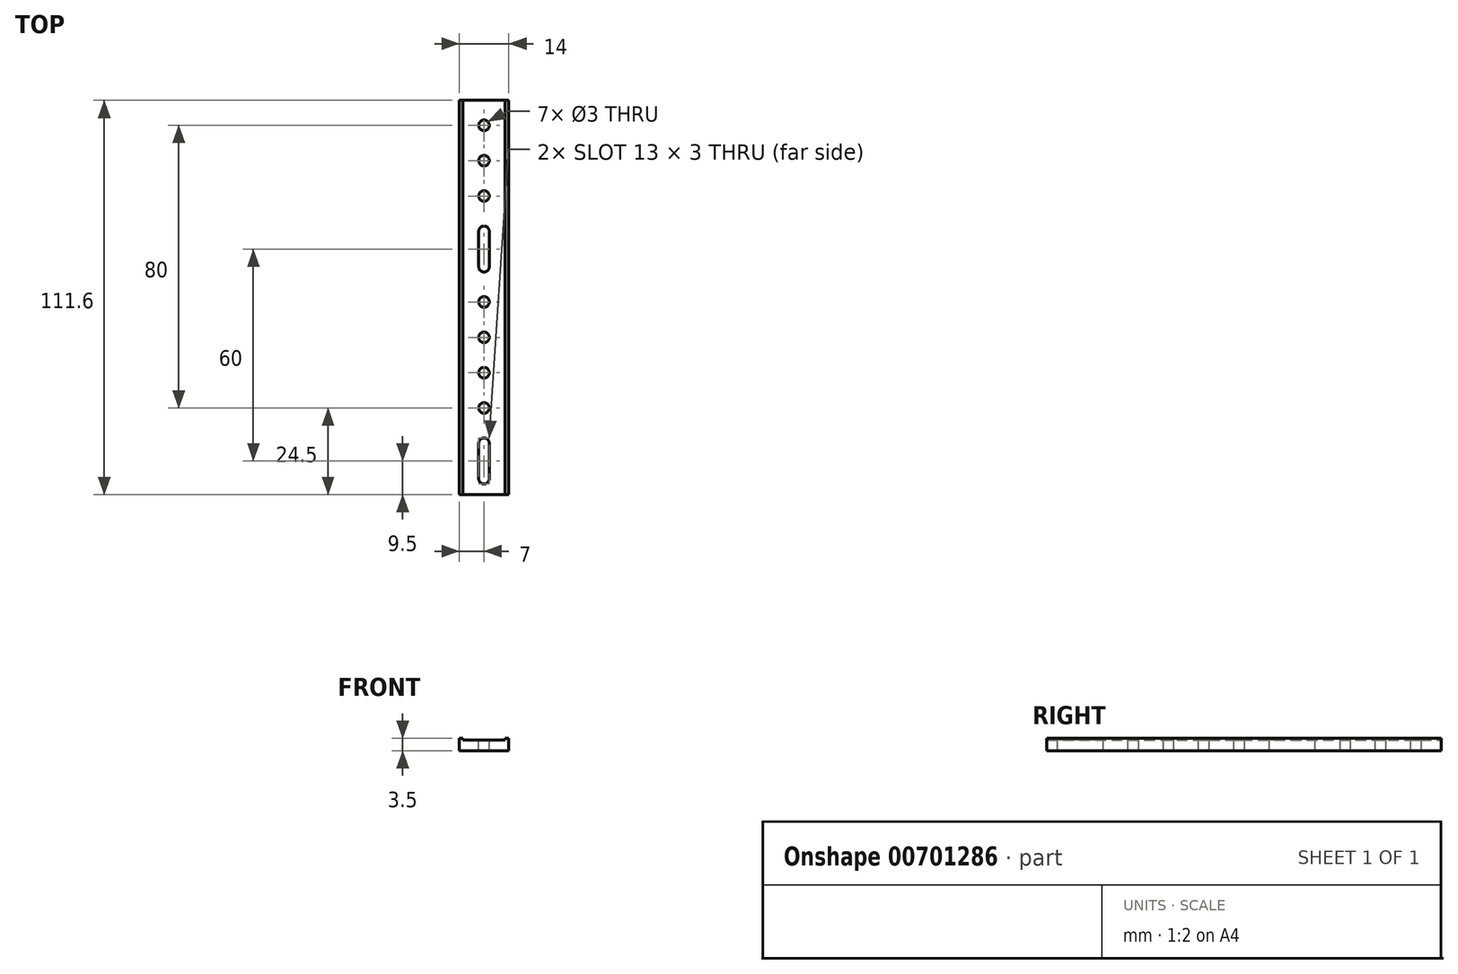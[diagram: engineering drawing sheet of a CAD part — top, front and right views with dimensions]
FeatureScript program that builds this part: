
annotation { "Feature Type Name" : "Feature", "Feature Type Description" : "" }
export const myFeature = defineFeature(function(context is Context, id is Id, definition is map)
    precondition{}
    {
        {
            var Q0;
            Q0=qCreatedBy(makeId("Top.planeOp"),FACE);
            var sketch = newSketch(context, id + "F0", { "sketchPlane" : qUnion([Q0])});
            skLineSegment(sketch, "E0.bottom", {"start": v(0, 0) * mm, "end": v(14, 0) * mm});
            skLineSegment(sketch, "E0.top", {"start": v(0, 111.6) * mm, "end": v(14, 111.6) * mm});
            skLineSegment(sketch, "E0.left", {"start": v(0, 0) * mm, "end": v(0, 111.6) * mm});
            skLineSegment(sketch, "E0.right", {"start": v(14, 0) * mm, "end": v(14, 111.6) * mm});
            skSolve(sketch);
        }
        {
            var Q0;
            Q0 = qSketchRegion(id + "F0", true);
            extrude(context, id + "F1", {"entities" : qUnion([Q0]), "depth" : 3 * mm, "offsetDistance" : 25 * mm});
        }
        {
            var Q0;
            Q0=makeQuery(id+"F1.opExtrude","CAP_FACE",FACE,{"disambiguationData":[OSD([sQuery(id+"F0.wireOp",EDGE,"E0.bottom"),sQuery(id+"F0.wireOp",EDGE,"E0.top"),sQuery(id+"F0.wireOp",EDGE,"E0.left"),sQuery(id+"F0.wireOp",EDGE,"E0.right")])],"isStart":false});
            var sketch = newSketch(context, id + "F2", { "sketchPlane" : qUnion([Q0])});
            skLineSegment(sketch, "E1.bottom", {"start": v(0, 0) * mm, "end": v(1, 0) * mm});
            skLineSegment(sketch, "E1.top", {"start": v(0, 111.6) * mm, "end": v(1, 111.6) * mm});
            skLineSegment(sketch, "E1.left", {"start": v(0, 0) * mm, "end": v(0, 111.6) * mm});
            skLineSegment(sketch, "E1.right", {"start": v(1, 0) * mm, "end": v(1, 111.6) * mm});
            skLineSegment(sketch, "E2.bottom", {"start": v(14, 0) * mm, "end": v(13, 0) * mm});
            skLineSegment(sketch, "E2.top", {"start": v(14, 111.6) * mm, "end": v(13, 111.6) * mm});
            skLineSegment(sketch, "E2.left", {"start": v(14, 0) * mm, "end": v(14, 111.6) * mm});
            skLineSegment(sketch, "E2.right", {"start": v(13, 0) * mm, "end": v(13, 111.6) * mm});
            skSolve(sketch);
        }
        {
            var Q0;
            Q0 = qSketchRegion(id + "F2", true);
            extrude(context, id + "F3", {"entities" : qUnion([Q0]), "operationType" : NewBodyOperationType.ADD, "depth" : 0.5 * mm, "offsetDistance" : 25 * mm});
        }
        {
            var Q0;
            Q0=makeQuery(id+"F1.opExtrude","CAP_FACE",FACE,{"disambiguationData":[OSD([sQuery(id+"F0.wireOp",EDGE,"E0.bottom"),sQuery(id+"F0.wireOp",EDGE,"E0.top"),sQuery(id+"F0.wireOp",EDGE,"E0.left"),sQuery(id+"F0.wireOp",EDGE,"E0.right")])],"isStart":false});
            var sketch = newSketch(context, id + "F4", { "sketchPlane" : qUnion([Q0])});
            skArc(sketch, "E3", {"start": v(5.5, 4.5) * mm, "mid": v(7, 3) * mm, "end": v(8.5, 4.5) * mm});
            skArc(sketch, "E4", {"start": v(8.5, 14.5) * mm, "mid": v(7, 16) * mm, "end": v(5.5, 14.5) * mm});
            skLineSegment(sketch, "E5", {"start": v(8.5, 4.5) * mm, "end": v(8.5, 14.5) * mm});
            skLineSegment(sketch, "E6", {"start": v(5.5, 14.5) * mm, "end": v(5.5, 4.5) * mm});
            skCircle(sketch, "E7", {"center": v(7, 24.5) * mm, "radius": 1.5 * mm});
            skCircle(sketch, "E8", {"center": v(7, 34.5) * mm, "radius": 1.5 * mm});
            skCircle(sketch, "E9", {"center": v(7, 44.5) * mm, "radius": 1.5 * mm});
            skCircle(sketch, "E10", {"center": v(7, 54.5) * mm, "radius": 1.5 * mm});
            skArc(sketch, "E11", {"start": v(5.5, 64.5) * mm, "mid": v(7, 63) * mm, "end": v(8.5, 64.5) * mm});
            skLineSegment(sketch, "E12", {"start": v(5.5, 64.5) * mm, "end": v(5.5, 74.5) * mm});
            skLineSegment(sketch, "E13", {"start": v(8.5, 64.5) * mm, "end": v(8.5, 74.5) * mm});
            skCircle(sketch, "E14", {"center": v(7, 84.5) * mm, "radius": 1.5 * mm});
            skCircle(sketch, "E15", {"center": v(7, 94.5) * mm, "radius": 1.5 * mm});
            skCircle(sketch, "E16", {"center": v(7, 104.5) * mm, "radius": 1.5 * mm});
            skPoint(sketch, "E17.orphan", {"position": v(7, 0) * mm});
            skPoint(sketch, "E18.orphan", {"position": v(7, 16) * mm});
            skPoint(sketch, "E19.start.orphan", {"position": v(7, 23) * mm});
            skPoint(sketch, "E20.orphan", {"position": v(7, 33) * mm});
            skPoint(sketch, "E21.orphan", {"position": v(7, 36) * mm});
            skPoint(sketch, "E22.orphan", {"position": v(7, 43) * mm});
            skPoint(sketch, "E23.orphan", {"position": v(7, 46) * mm});
            skPoint(sketch, "E24.orphan", {"position": v(7, 53) * mm});
            skPoint(sketch, "E25.orphan", {"position": v(7, 56) * mm});
            skPoint(sketch, "E26.orphan", {"position": v(7, 63) * mm});
            skArc(sketch, "E27", {"start": v(8.5, 74.5) * mm, "mid": v(7, 76) * mm, "end": v(5.5, 74.5) * mm});
            skPoint(sketch, "E28.orphan", {"position": v(7, 76) * mm});
            skPoint(sketch, "E29.trimOffspring.start.orphan", {"position": v(7, 83) * mm});
            skPoint(sketch, "E30.start.orphan", {"position": v(7, 86) * mm});
            skPoint(sketch, "E31.orphan", {"position": v(7, 93) * mm});
            skPoint(sketch, "E32.orphan", {"position": v(7, 96) * mm});
            skPoint(sketch, "E33.orphan", {"position": v(7, 103) * mm});
            skPoint(sketch, "E34.end.orphan", {"position": v(7, 111.6) * mm});
            skPoint(sketch, "E34.start.orphan", {"position": v(7, 106) * mm});
            skSolve(sketch);
        }
        {
            var Q0;
            Q0 = qSketchRegion(id + "F4", true);
            extrude(context, id + "F5", {"entities" : qUnion([Q0]), "operationType" : NewBodyOperationType.REMOVE, "oppositeDirection" : true, "depth" : 25 * mm, "offsetDistance" : 25 * mm});
        }
    });
